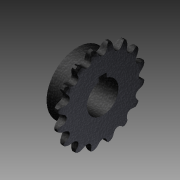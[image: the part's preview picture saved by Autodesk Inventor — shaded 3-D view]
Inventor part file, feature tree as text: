
AUTODESK INVENTOR PART (.ipt)
format: ipt  version: 2012 (Build 160160000, 160)  size: 976,896 bytes
history: native  units: in
note: dims shown in document units (in); Inventor stores cm internally (conversion verified against a paired STEP export)
features: extrude x2, imported_body x1, sketch x1
ambient origin geometry x8: Origin, YZ Plane, XZ Plane, XY Plane, X Axis, Y Axis, Z Axis, Center Point
bodies: Solid1 (feature_tree)
feature tree (4):
  imported_body  "Base1"
  sketch  "Sketch1"  dims[d0=0.5in d1=1.0in d2=0.0in d5=0.125in d7=0.0625in d8=0.3125in d9=0.125in d10=1.0in d11=0.0in]
  extrude  "Extrusion1"  Depth=1.0in TaperAngle=0.0deg
  extrude  "Extrusion2"  Depth=0.125in
